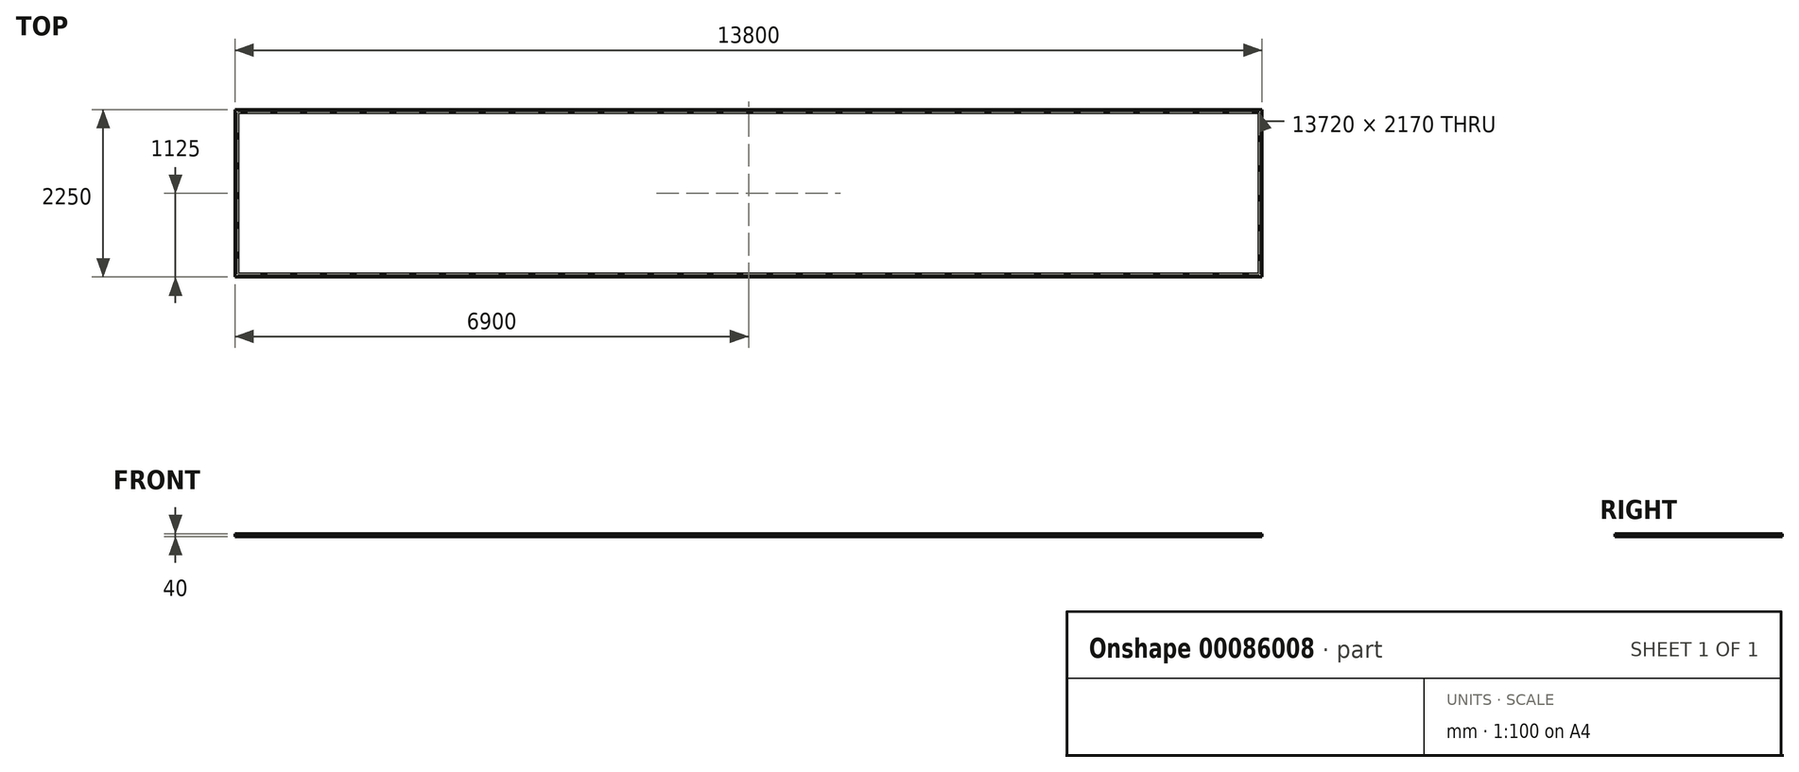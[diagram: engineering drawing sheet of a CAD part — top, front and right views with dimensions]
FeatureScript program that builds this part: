
annotation { "Feature Type Name" : "Feature", "Feature Type Description" : "" }
export const myFeature = defineFeature(function(context is Context, id is Id, definition is map)
    precondition{}
    {
        {
            var Q0;
            Q0=qCreatedBy(makeId("Top.planeOp"),FACE);
            var sketch = newSketch(context, id + "F0", { "sketchPlane" : qUnion([Q0])});
            skLineSegment(sketch, "E0.bottom", {"start": v(6900, 1125) * mm, "end": v(-6900, 1125) * mm});
            skLineSegment(sketch, "E0.top", {"start": v(6900, -1125) * mm, "end": v(-6900, -1125) * mm});
            skLineSegment(sketch, "E0.left", {"start": v(6900, 1125) * mm, "end": v(6900, -1125) * mm});
            skLineSegment(sketch, "E0.right", {"start": v(-6900, 1125) * mm, "end": v(-6900, -1125) * mm});
            skPoint(sketch, "E0.middle", {"position": v(0, 0) * mm});
            skLineSegment(sketch, "E1.bottom", {"start": v(6860, 1085) * mm, "end": v(-6860, 1085) * mm});
            skLineSegment(sketch, "E1.top", {"start": v(6860, -1085) * mm, "end": v(-6860, -1085) * mm});
            skLineSegment(sketch, "E1.left", {"start": v(6860, 1085) * mm, "end": v(6860, -1085) * mm});
            skLineSegment(sketch, "E1.right", {"start": v(-6860, 1085) * mm, "end": v(-6860, -1085) * mm});
            skLineSegment(sketch, "E2.bottom", {"start": v(-5200, 1085) * mm, "end": v(-5160, 1085) * mm});
            skLineSegment(sketch, "E2.top", {"start": v(-5200, -1085) * mm, "end": v(-5160, -1085) * mm});
            skLineSegment(sketch, "E2.left", {"start": v(-5200, 1085) * mm, "end": v(-5200, -1085) * mm});
            skLineSegment(sketch, "E2.right", {"start": v(-5160, 1085) * mm, "end": v(-5160, -1085) * mm});
            skLineSegment(sketch, "E3.bottom", {"start": v(-3500, 1085) * mm, "end": v(-3460, 1085) * mm});
            skLineSegment(sketch, "E3.top", {"start": v(-3500, -1085) * mm, "end": v(-3460, -1085) * mm});
            skLineSegment(sketch, "E3.left", {"start": v(-3500, 1085) * mm, "end": v(-3500, -1085) * mm});
            skLineSegment(sketch, "E3.right", {"start": v(-3460, 1085) * mm, "end": v(-3460, -1085) * mm});
            skLineSegment(sketch, "E4.bottom", {"start": v(-1800, 1085) * mm, "end": v(-1760, 1085) * mm});
            skLineSegment(sketch, "E4.top", {"start": v(-1800, -1085) * mm, "end": v(-1760, -1085) * mm});
            skLineSegment(sketch, "E4.left", {"start": v(-1760, 1085) * mm, "end": v(-1760, -1085) * mm});
            skLineSegment(sketch, "E4.right", {"start": v(-1800, 1085) * mm, "end": v(-1800, -1085) * mm});
            skLineSegment(sketch, "E5.bottom", {"start": v(1600, 1085) * mm, "end": v(1640, 1085) * mm});
            skLineSegment(sketch, "E5.top", {"start": v(1600, -1085) * mm, "end": v(1640, -1085) * mm});
            skLineSegment(sketch, "E5.left", {"start": v(1600, 1085) * mm, "end": v(1600, -1085) * mm});
            skLineSegment(sketch, "E5.right", {"start": v(1640, 1085) * mm, "end": v(1640, -1085) * mm});
            skLineSegment(sketch, "E6.bottom", {"start": v(3300, 1085) * mm, "end": v(3340, 1085) * mm});
            skLineSegment(sketch, "E6.top", {"start": v(3300, -1085) * mm, "end": v(3340, -1085) * mm});
            skLineSegment(sketch, "E6.left", {"start": v(3300, 1085) * mm, "end": v(3300, -1085) * mm});
            skLineSegment(sketch, "E6.right", {"start": v(3340, 1085) * mm, "end": v(3340, -1085) * mm});
            skLineSegment(sketch, "E7.bottom", {"start": v(-100, 1085) * mm, "end": v(-60, 1085) * mm});
            skLineSegment(sketch, "E7.top", {"start": v(-100, -1085) * mm, "end": v(-60, -1085) * mm});
            skLineSegment(sketch, "E7.left", {"start": v(-100, 1085) * mm, "end": v(-100, -1085) * mm});
            skLineSegment(sketch, "E7.right", {"start": v(-60, 1085) * mm, "end": v(-60, -1085) * mm});
            skLineSegment(sketch, "E8.bottom", {"start": v(5000, 1085) * mm, "end": v(5040, 1085) * mm});
            skLineSegment(sketch, "E8.top", {"start": v(5000, -1085) * mm, "end": v(5040, -1085) * mm});
            skLineSegment(sketch, "E8.left", {"start": v(5000, 1085) * mm, "end": v(5000, -1085) * mm});
            skLineSegment(sketch, "E8.right", {"start": v(5040, 1085) * mm, "end": v(5040, -1085) * mm});
            skSolve(sketch);
        }
        {
            var Q0;
            Q0=makeQuery(id+"F0.imprint","IMPRINT",FACE,{"disambiguationData":[TD([[makeQuery(id+"F0.imprint","IMPRINT",EDGE,{"derivedFrom":sQuery(id+"F0.wireOp",EDGE,"E2.bottom")}),-1.0]])]});
            var Q1;
            Q1=makeQuery(id+"F0.imprint","IMPRINT",FACE,{"disambiguationData":[TD([[makeQuery(id+"F0.imprint","IMPRINT",EDGE,{"derivedFrom":sQuery(id+"F0.wireOp",EDGE,"E3.bottom")}),-1.0]])]});
            var Q2;
            Q2=makeQuery(id+"F0.imprint","IMPRINT",FACE,{"disambiguationData":[TD([[makeQuery(id+"F0.imprint","IMPRINT",EDGE,{"derivedFrom":sQuery(id+"F0.wireOp",EDGE,"E0.bottom")}),1.0]])]});
            var Q3;
            Q3=makeQuery(id+"F0.imprint","IMPRINT",FACE,{"disambiguationData":[TD([[makeQuery(id+"F0.imprint","IMPRINT",EDGE,{"derivedFrom":sQuery(id+"F0.wireOp",EDGE,"E4.bottom")}),-1.0]])]});
            var Q4;
            Q4=makeQuery(id+"F0.imprint","IMPRINT",FACE,{"disambiguationData":[TD([[makeQuery(id+"F0.imprint","IMPRINT",EDGE,{"derivedFrom":sQuery(id+"F0.wireOp",EDGE,"E7.bottom")}),-1.0]])]});
            var Q5;
            Q5=makeQuery(id+"F0.imprint","IMPRINT",FACE,{"disambiguationData":[TD([[makeQuery(id+"F0.imprint","IMPRINT",EDGE,{"derivedFrom":sQuery(id+"F0.wireOp",EDGE,"E5.bottom")}),-1.0]])]});
            var Q6;
            Q6=makeQuery(id+"F0.imprint","IMPRINT",FACE,{"disambiguationData":[TD([[makeQuery(id+"F0.imprint","IMPRINT",EDGE,{"derivedFrom":sQuery(id+"F0.wireOp",EDGE,"E6.bottom")}),-1.0]])]});
            var Q7;
            Q7=makeQuery(id+"F0.imprint","IMPRINT",FACE,{"disambiguationData":[TD([[makeQuery(id+"F0.imprint","IMPRINT",EDGE,{"derivedFrom":sQuery(id+"F0.wireOp",EDGE,"E8.bottom")}),-1.0]])]});
            extrude(context, id + "F1", {"entities" : qUnion([Q0, Q1, Q2, Q3, Q4, Q5, Q6, Q7]), "oppositeDirection" : true, "depth" : 40 * mm});
        }
    });
